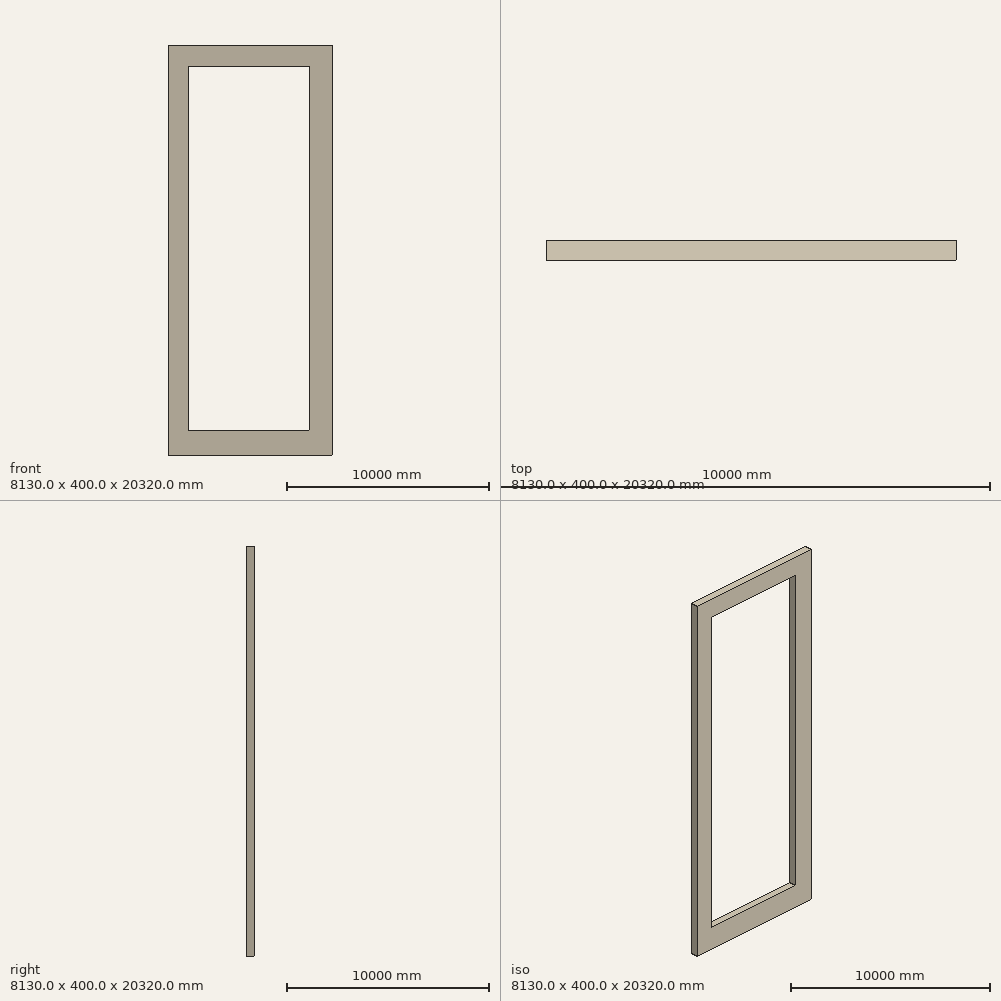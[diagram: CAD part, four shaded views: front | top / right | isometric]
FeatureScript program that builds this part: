
annotation { "Feature Type Name" : "Feature", "Feature Type Description" : "" }
export const myFeature = defineFeature(function(context is Context, id is Id, definition is map)
    precondition{}
    {
        {
            var Q0;
            Q0=qCreatedBy(makeId("Front.planeOp"),FACE);
            var sketch = newSketch(context, id + "F0", { "sketchPlane" : qUnion([Q0])});
            skLineSegment(sketch, "E0.bottom", {"start": v(-4063.27, 15117.34) * mm, "end": v(4066.73, 15117.34) * mm});
            skLineSegment(sketch, "E0.top", {"start": v(-4063.27, -5202.66) * mm, "end": v(4066.73, -5202.66) * mm});
            skLineSegment(sketch, "E0.left", {"start": v(-4063.27, 15117.34) * mm, "end": v(-4063.27, -5202.66) * mm});
            skLineSegment(sketch, "E0.right", {"start": v(4066.73, 15117.34) * mm, "end": v(4066.73, -5202.66) * mm});
            skLineSegment(sketch, "E1.bottom", {"start": v(-3073.27, 14057.34) * mm, "end": v(2926.73, 14057.34) * mm});
            skLineSegment(sketch, "E1.top", {"start": v(-3073.27, -3942.66) * mm, "end": v(2926.73, -3942.66) * mm});
            skLineSegment(sketch, "E1.left", {"start": v(-3073.27, 14057.34) * mm, "end": v(-3073.27, -3942.66) * mm});
            skLineSegment(sketch, "E1.right", {"start": v(2926.73, 14057.34) * mm, "end": v(2926.73, -3942.66) * mm});
            skSolve(sketch);
        }
        {
            var Q0;
            Q0=makeQuery(id+"F0.imprint","IMPRINT",FACE,{"disambiguationData":[TD([[makeQuery(id+"F0.imprint","IMPRINT",EDGE,{"derivedFrom":sQuery(id+"F0.wireOp",EDGE,"E0.bottom")}),-1.0]])]});
            extrude(context, id + "F1", {"entities" : qUnion([Q0]), "endBound" : BoundingType.SYMMETRIC, "depth" : 400 * mm, "offsetDistance" : 25 * mm});
        }
    });
